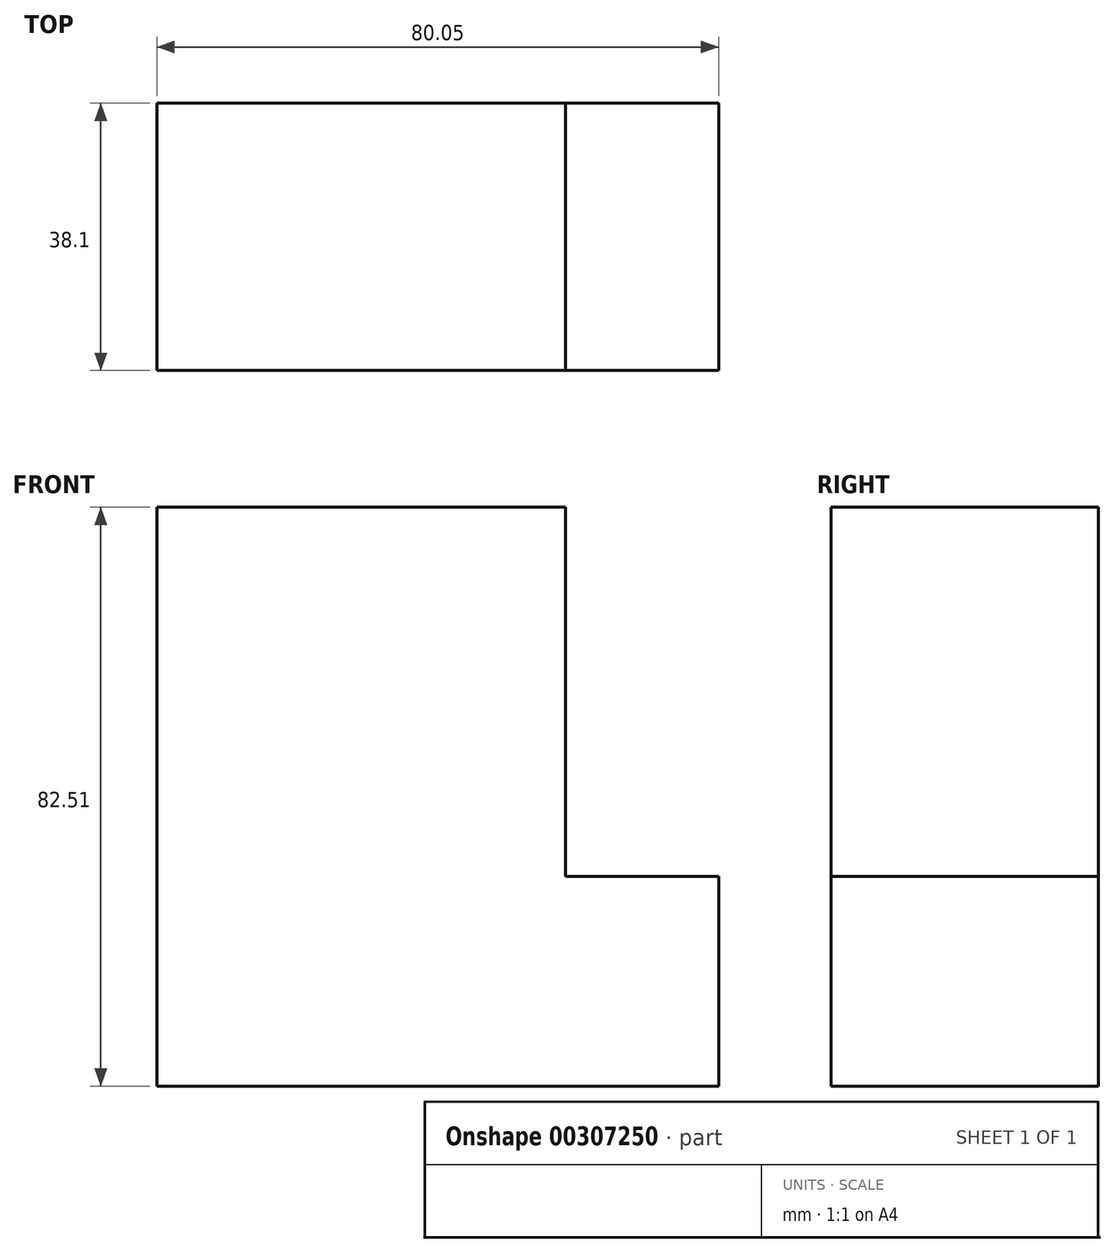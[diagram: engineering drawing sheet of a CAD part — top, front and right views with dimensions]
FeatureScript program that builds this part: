
annotation { "Feature Type Name" : "Feature", "Feature Type Description" : "" }
export const myFeature = defineFeature(function(context is Context, id is Id, definition is map)
    precondition{}
    {
        {
            var Q0;
            Q0=qCreatedBy(makeId("Front.planeOp"),FACE);
            var sketch = newSketch(context, id + "F0", { "sketchPlane" : qUnion([Q0])});
            skLineSegment(sketch, "E0", {"start": v(11.58, -14.36) * mm, "end": v(11.58, 38.27) * mm});
            skLineSegment(sketch, "E1", {"start": v(11.58, 38.27) * mm, "end": v(-46.67, 38.27) * mm});
            skLineSegment(sketch, "E2", {"start": v(-46.67, -44.24) * mm, "end": v(-46.67, 38.27) * mm});
            skLineSegment(sketch, "E3", {"start": v(-46.67, -44.24) * mm, "end": v(33.38, -44.24) * mm});
            skLineSegment(sketch, "E4", {"start": v(33.38, -44.24) * mm, "end": v(33.38, -14.36) * mm});
            skLineSegment(sketch, "E5", {"start": v(33.38, -14.36) * mm, "end": v(11.58, -14.36) * mm});
            skSolve(sketch);
        }
        {
            var Q0;
            Q0=makeQuery(id+"F0.imprint","IMPRINT",FACE,{"disambiguationData":[TD([[makeQuery(id+"F0.imprint","IMPRINT",EDGE,{"derivedFrom":sQuery(id+"F0.wireOp",EDGE,"E0")}),1.0]])]});
            extrude(context, id + "F1", {"entities" : qUnion([Q0]), "depth" : 38.1 * mm});
        }
    });
